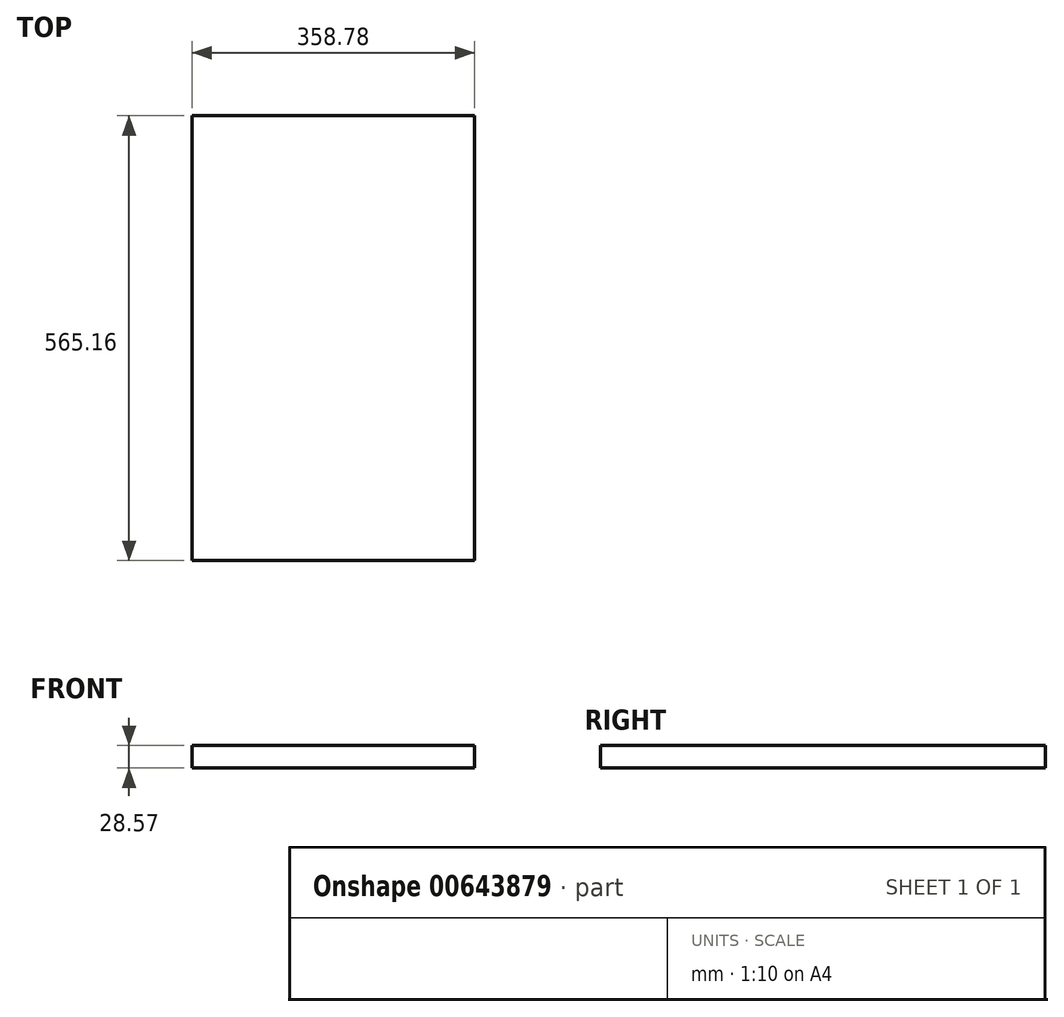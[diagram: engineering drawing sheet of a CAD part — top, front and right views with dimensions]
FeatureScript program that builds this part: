
annotation { "Feature Type Name" : "Feature", "Feature Type Description" : "" }
export const myFeature = defineFeature(function(context is Context, id is Id, definition is map)
    precondition{}
    {
        {
            var Q0;
            Q0=qCreatedBy(makeId("Top.planeOp"),FACE);
            var sketch = newSketch(context, id + "F0", { "sketchPlane" : qUnion([Q0])});
            skLineSegment(sketch, "E0.bottom", {"start": v(-179.39, 282.58) * mm, "end": v(179.39, 282.58) * mm});
            skLineSegment(sketch, "E0.top", {"start": v(-179.39, -282.58) * mm, "end": v(179.39, -282.58) * mm});
            skLineSegment(sketch, "E0.left", {"start": v(-179.39, 282.58) * mm, "end": v(-179.39, -282.58) * mm});
            skLineSegment(sketch, "E0.right", {"start": v(179.39, 282.58) * mm, "end": v(179.39, -282.58) * mm});
            skPoint(sketch, "E0.middle", {"position": v(0, 0) * mm});
            skSolve(sketch);
        }
        {
            var Q0;
            Q0=makeQuery(id+"F0.imprint","IMPRINT",FACE,{"disambiguationData":[TD([[makeQuery(id+"F0.imprint","IMPRINT",EDGE,{"derivedFrom":sQuery(id+"F0.wireOp",EDGE,"E0.bottom")}),-1.0]])]});
            extrude(context, id + "F1", {"entities" : qUnion([Q0]), "depth" : 28.57 * mm, "offsetDistance" : 25.4 * mm});
        }
    });
